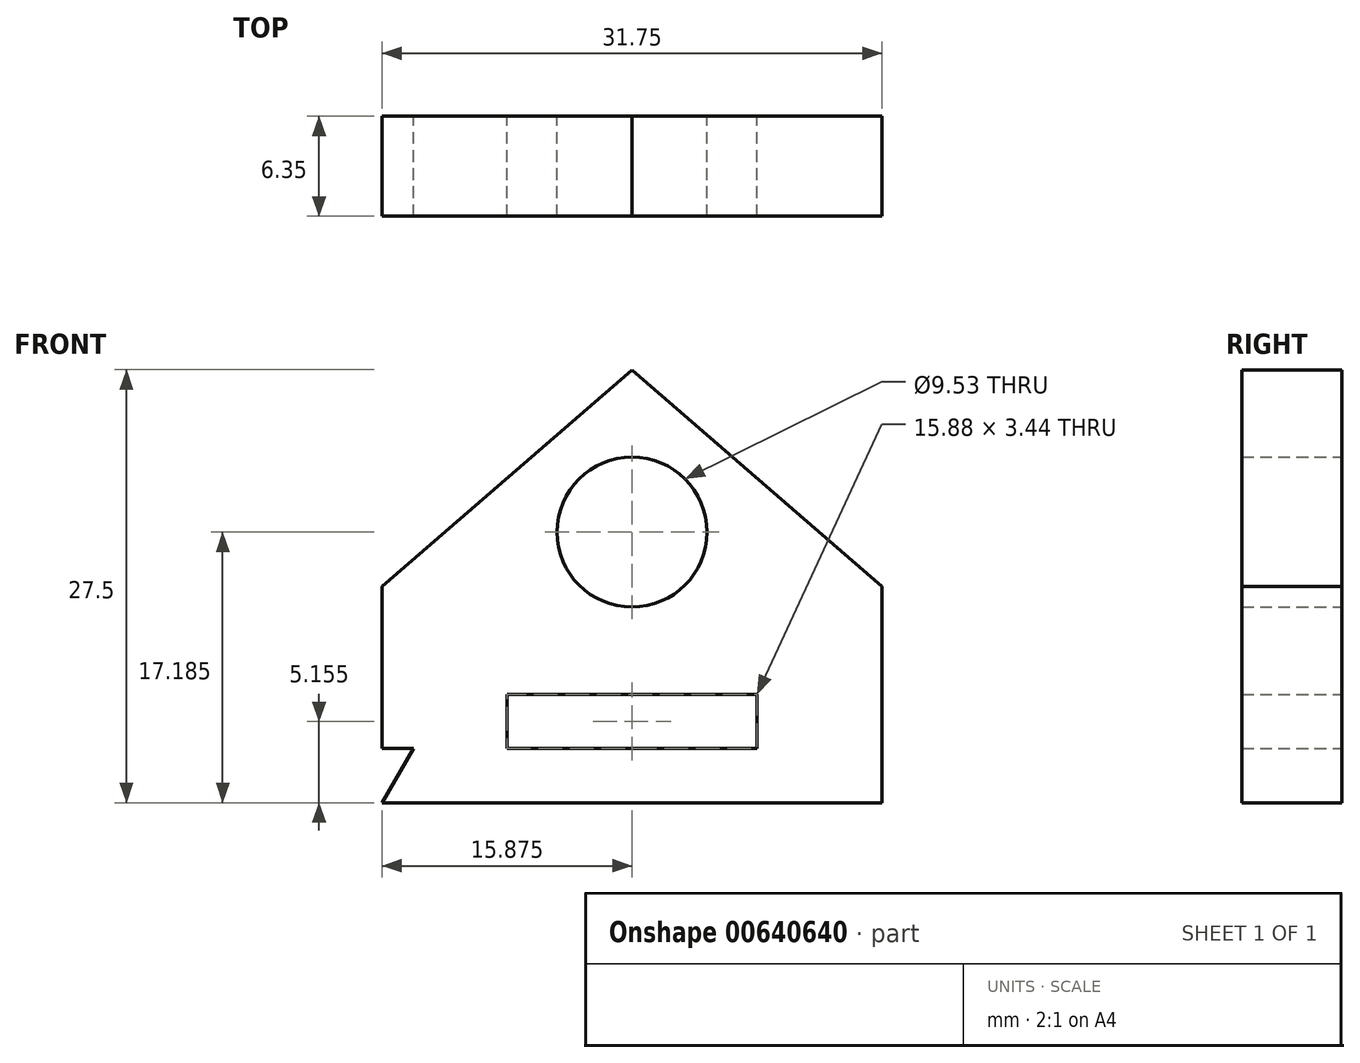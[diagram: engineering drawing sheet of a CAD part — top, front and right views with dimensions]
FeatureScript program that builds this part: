
annotation { "Feature Type Name" : "Feature", "Feature Type Description" : "" }
export const myFeature = defineFeature(function(context is Context, id is Id, definition is map)
    precondition{}
    {
        {
            var Q0;
            Q0=qCreatedBy(makeId("Front.planeOp"),FACE);
            var sketch = newSketch(context, id + "F0", { "sketchPlane" : qUnion([Q0])});
            skLineSegment(sketch, "E0", {"start": v(0, 0) * mm, "end": v(31.75, 0) * mm});
            skLineSegment(sketch, "E1", {"start": v(0, 0) * mm, "end": v(15.88, 27.5) * mm});
            skLineSegment(sketch, "E2", {"start": v(15.88, 27.5) * mm, "end": v(31.75, 0) * mm});
            skLineSegment(sketch, "E3", {"start": v(7.94, 13.75) * mm, "end": v(0, 13.75) * mm});
            skLineSegment(sketch, "E4", {"start": v(0, 13.75) * mm, "end": v(0, 0) * mm});
            skLineSegment(sketch, "E5", {"start": v(0, 13.75) * mm, "end": v(15.88, 27.5) * mm});
            skLineSegment(sketch, "E6", {"start": v(23.81, 13.75) * mm, "end": v(31.75, 13.75) * mm});
            skLineSegment(sketch, "E7", {"start": v(31.75, 13.75) * mm, "end": v(31.75, 0) * mm});
            skLineSegment(sketch, "E8", {"start": v(31.75, 13.75) * mm, "end": v(15.88, 27.5) * mm});
            skLineSegment(sketch, "E9", {"start": v(7.94, 13.75) * mm, "end": v(23.81, 13.75) * mm});
            skCircle(sketch, "E10", {"center": v(15.88, 17.19) * mm, "radius": 4.76 * mm});
            skLineSegment(sketch, "E11", {"start": v(0, 6.87) * mm, "end": v(0, 0) * mm});
            skLineSegment(sketch, "E12", {"start": v(0, 3.44) * mm, "end": v(31.75, 3.44) * mm});
            skLineSegment(sketch, "E13", {"start": v(15.88, 3.44) * mm, "end": v(29.77, 3.44) * mm});
            skLineSegment(sketch, "E14", {"start": v(29.77, 3.44) * mm, "end": v(1.98, 3.44) * mm});
            skLineSegment(sketch, "E15", {"start": v(0, 0) * mm, "end": v(15.88, 0) * mm});
            skLineSegment(sketch, "E16", {"start": v(15.88, 0) * mm, "end": v(7.94, 0) * mm});
            skLineSegment(sketch, "E17", {"start": v(15.88, 0) * mm, "end": v(31.75, 0) * mm});
            skLineSegment(sketch, "E18", {"start": v(11.9, 3.44) * mm, "end": v(15.88, 3.44) * mm});
            skLineSegment(sketch, "E19", {"start": v(15.88, 6.87) * mm, "end": v(12.7, 6.87) * mm});
            skLineSegment(sketch, "E20", {"start": v(15.88, 6.87) * mm, "end": v(19.05, 6.87) * mm});
            skLineSegment(sketch, "E21", {"start": v(12.7, 6.87) * mm, "end": v(12.7, 3.44) * mm});
            skLineSegment(sketch, "E22", {"start": v(12.7, 3.44) * mm, "end": v(19.05, 3.44) * mm});
            skLineSegment(sketch, "E23", {"start": v(19.05, 3.44) * mm, "end": v(19.05, 6.87) * mm});
            skLineSegment(sketch, "E24", {"start": v(12.7, 6.87) * mm, "end": v(7.94, 6.87) * mm});
            skLineSegment(sketch, "E25", {"start": v(19.05, 6.87) * mm, "end": v(23.81, 6.87) * mm});
            skLineSegment(sketch, "E26.bottom", {"start": v(7.94, 6.87) * mm, "end": v(12.7, 6.87) * mm});
            skLineSegment(sketch, "E26.top", {"start": v(7.94, 3.44) * mm, "end": v(12.7, 3.44) * mm});
            skLineSegment(sketch, "E26.left", {"start": v(7.94, 6.87) * mm, "end": v(7.94, 3.44) * mm});
            skLineSegment(sketch, "E27.bottom", {"start": v(23.81, 6.87) * mm, "end": v(19.05, 6.87) * mm});
            skLineSegment(sketch, "E27.top", {"start": v(23.81, 3.44) * mm, "end": v(19.05, 3.44) * mm});
            skLineSegment(sketch, "E27.left", {"start": v(23.81, 6.87) * mm, "end": v(23.81, 3.44) * mm});
            skLineSegment(sketch, "E27.right", {"start": v(19.05, 6.87) * mm, "end": v(19.05, 3.44) * mm});
            skLineSegment(sketch, "E28.bottom", {"start": v(12.7, 6.87) * mm, "end": v(19.05, 6.87) * mm});
            skSolve(sketch);
        }
        {
            var Q0;
            {var subQ2=sQuery(id+"F0.wireOp",EDGE,"E3");Q0=makeQuery(id+"F0.imprint","IMPRINT",FACE,{"disambiguationData":[TD([[makeQuery(id+"F0.imprint","IMPRINT",EDGE,{"derivedFrom":subQ2}),-1.0]])]});}
            var Q1;
            {var subQ0=sQuery(id+"F0.wireOp",EDGE,"E3");Q1=makeQuery(id+"F0.imprint","IMPRINT",FACE,{"disambiguationData":[TD([[makeQuery(id+"F0.imprint","IMPRINT",EDGE,{"derivedFrom":subQ0}),1.0]])]});}
            var Q2;
            {var subQ0=sQuery(id+"F0.wireOp",EDGE,"E15");Q2=makeQuery(id+"F0.imprint","IMPRINT",FACE,{"disambiguationData":[TD([[makeQuery(id+"F0.imprint","IMPRINT",EDGE,{"derivedFrom":subQ0}),1.0]])]});}
            var Q3;
            {var subQ5=sQuery(id+"F0.wireOp",EDGE,"yYBxNw9v-MzwS-UWZy-JpHA-7RBz7uhKMua0");Q3=makeQuery(id+"F0.imprint","IMPRINT",FACE,{"disambiguationData":[TD([[makeQuery(id+"F0.imprint","IMPRINT",EDGE,{"derivedFrom":subQ5}),1.0]])]});}
            var Q4;
            {var subQ0=sQuery(id+"F0.wireOp",EDGE,"dZJu9Jtc-TncH-VoL2-8lB4-W5X3L4HCVTCp");Q4=makeQuery(id+"F0.imprint","IMPRINT",FACE,{"disambiguationData":[TD([[makeQuery(id+"F0.imprint","IMPRINT",EDGE,{"derivedFrom":subQ0}),-1.0]])]});}
            var Q5;
            {var subQ0=sQuery(id+"F0.wireOp",EDGE,"dZJu9Jtc-TncH-VoL2-8lB4-W5X3L4HCVTCp");Q5=makeQuery(id+"F0.imprint","IMPRINT",FACE,{"disambiguationData":[TD([[makeQuery(id+"F0.imprint","IMPRINT",EDGE,{"derivedFrom":subQ0}),1.0]])]});}
            var Q6;
            {var subQ12=sQuery(id+"F0.wireOp",EDGE,"E10");var subQ13=sQuery(id+"F0.wireOp",EDGE,"E9");var subQ14=makeQuery(id+"F0.imprint","INTERSECT",VERTEX,{"disambiguationData":[OD(0.0)],"derivedFrom":[subQ13,subQ12]});Q6=makeQuery(id+"F0.imprint","IMPRINT",FACE,{"disambiguationData":[TD([[makeQuery(id+"F0.imprint","IMPRINT",EDGE,{"disambiguationData":[TD([[subQ14,-1.0]])],"derivedFrom":subQ12}),-1.0]])]});}
            var Q7;
            {var subQ0=sQuery(id+"F0.wireOp",EDGE,"E9");var subQ3=sQuery(id+"F0.wireOp",EDGE,"E10");var subQ4=makeQuery(id+"F0.imprint","INTERSECT",VERTEX,{"disambiguationData":[OD(0.0)],"derivedFrom":[subQ0,subQ3]});Q7=makeQuery(id+"F0.imprint","IMPRINT",FACE,{"disambiguationData":[TD([[makeQuery(id+"F0.imprint","IMPRINT",EDGE,{"disambiguationData":[TD([[subQ4,1.0]])],"derivedFrom":subQ3}),-1.0]])]});}
            var Q8;
            {var subQ2=sQuery(id+"F0.wireOp",EDGE,"E6");Q8=makeQuery(id+"F0.imprint","IMPRINT",FACE,{"disambiguationData":[TD([[makeQuery(id+"F0.imprint","IMPRINT",EDGE,{"derivedFrom":subQ2}),1.0]])]});}
            var Q9;
            {var subQ0=sQuery(id+"F0.wireOp",EDGE,"E6");Q9=makeQuery(id+"F0.imprint","IMPRINT",FACE,{"disambiguationData":[TD([[makeQuery(id+"F0.imprint","IMPRINT",EDGE,{"derivedFrom":subQ0}),-1.0]])]});}
            var Q10;
            {var subQ3=sQuery(id+"F0.wireOp",EDGE,"NS26V9Zt-xuZW-bt5E-kPqw-eHo78fBTTWJa");var subQ5=sQuery(id+"F0.wireOp",EDGE,"E7");var subQ6=makeQuery(id+"F0.imprint","INTERSECT",VERTEX,{"derivedFrom":[subQ5,subQ3]});Q10=makeQuery(id+"F0.imprint","IMPRINT",FACE,{"disambiguationData":[TD([[makeQuery(id+"F0.imprint","IMPRINT",EDGE,{"disambiguationData":[TD([[subQ6,-1.0]])],"derivedFrom":subQ5}),-1.0]])]});}
            var Q11;
            {var subQ1=sQuery(id+"F0.wireOp",EDGE,"E2");var subQ3=sQuery(id+"F0.wireOp",EDGE,"NS26V9Zt-xuZW-bt5E-kPqw-eHo78fBTTWJa");var subQ4=makeQuery(id+"F0.imprint","INTERSECT",VERTEX,{"derivedFrom":[subQ1,subQ3]});Q11=makeQuery(id+"F0.imprint","IMPRINT",FACE,{"disambiguationData":[TD([[makeQuery(id+"F0.imprint","IMPRINT",EDGE,{"disambiguationData":[TD([[subQ4,-1.0]])],"derivedFrom":subQ1}),-1.0]])]});}
            var Q12;
            {var subQ0=sQuery(id+"F0.wireOp",EDGE,"E17");var subQ5=sQuery(id+"F0.wireOp",EDGE,"jtxSi6pC-KC4R-7AnM-aHOg-KoQUS80cYyQ9");var subQ6=makeQuery(id+"F0.imprint","INTERSECT",VERTEX,{"derivedFrom":[subQ0,subQ5]});Q12=makeQuery(id+"F0.imprint","IMPRINT",FACE,{"disambiguationData":[TD([[makeQuery(id+"F0.imprint","IMPRINT",EDGE,{"disambiguationData":[TD([[subQ6,-1.0]])],"derivedFrom":subQ5}),-1.0]])]});}
            var Q13;
            {var subQ0=sQuery(id+"F0.wireOp",EDGE,"E7");var subQ3=sQuery(id+"F0.wireOp",EDGE,"E12");var subQ5=makeQuery(id+"F0.imprint","INTERSECT",VERTEX,{"derivedFrom":[subQ0,subQ3]});Q13=makeQuery(id+"F0.imprint","IMPRINT",FACE,{"disambiguationData":[TD([[makeQuery(id+"F0.imprint","IMPRINT",EDGE,{"disambiguationData":[TD([[subQ5,-1.0]])],"derivedFrom":subQ0}),-1.0]])]});}
            var Q14;
            {var subQ9=sQuery(id+"F0.wireOp",EDGE,"E16");Q14=makeQuery(id+"F0.imprint","IMPRINT",FACE,{"disambiguationData":[TD([[makeQuery(id+"F0.imprint","IMPRINT",EDGE,{"derivedFrom":subQ9}),-1.0]])]});}
            var Q15;
            {var subQ0=sQuery(id+"F0.wireOp",EDGE,"E11");var subQ3=sQuery(id+"F0.wireOp",EDGE,"E12");var subQ5=makeQuery(id+"F0.imprint","INTERSECT",VERTEX,{"derivedFrom":[subQ0,subQ3]});Q15=makeQuery(id+"F0.imprint","IMPRINT",FACE,{"disambiguationData":[TD([[makeQuery(id+"F0.imprint","IMPRINT",EDGE,{"disambiguationData":[TD([[subQ5,-1.0]])],"derivedFrom":subQ0}),1.0]])]});}
            var Q16;
            Q16=makeQuery(id+"F0.imprint","IMPRINT",FACE,{"disambiguationData":[TD([[makeQuery(id+"F0.imprint","IMPRINT",EDGE,{"derivedFrom":sQuery(id+"F0.wireOp",EDGE,"E28.bottom")}),-1.0]])]});
            extrude(context, id + "F1", {"entities" : qUnion([Q0, Q1, Q2, Q3, Q4, Q5, Q6, Q7, Q8, Q9, Q10, Q11, Q12, Q13, Q14, Q15, Q16]), "depth" : 6.35 * mm, "offsetDistance" : 25.4 * mm});
        }
    });
